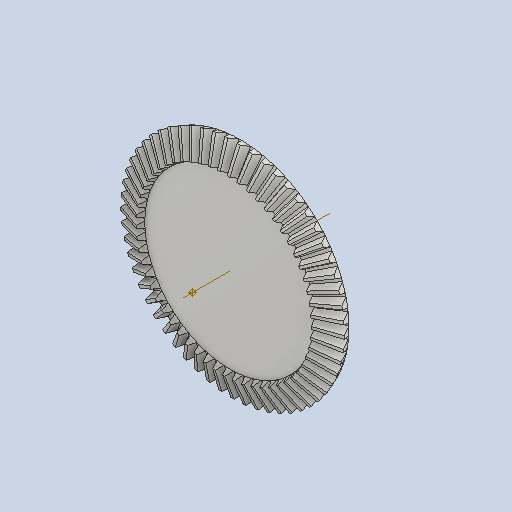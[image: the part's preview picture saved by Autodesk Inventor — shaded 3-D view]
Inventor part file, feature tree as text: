
AUTODESK INVENTOR PART (.ipt)
format: ipt  version: 2023 (Build 270158030, 158C)  size: 857,088 bytes
history: native  units: mm
features: other x24, loft x2, pattern_circular x2, sketch x1
ambient origin geometry x6: Origin, XZ Plane, X Axis, Y Axis, Z Axis, Center Point
bodies: Solid1 (feature_tree)
feature tree (29):
  other  "Top Point"
  other  "Mesh Plane2"
  other  "Teeth Body"
  other  "Start Point"
  other  "Tooth Plane"
  other  "Start Sketch"
  other  "End Point"
  other  "3D Sketch Right"
  other  "End Plane Right"
  loft  "Loft Right"
  pattern_circular  "Circular Pattern Right"  [2 undecoded]
  other  "3D Sketch Left"
  other  "End Plane Left"
  loft  "Loft Left"
  pattern_circular  "Circular Pattern Left"  [2 undecoded]
  other  "Fix Body"
  other  "Mesh Plane"
  other  "Top Plane"
  other  "Teeth Body Sketch"
  other  "End Plane"
  other  "End Sketch"
  other  "Helical Curve Left"
  other  "End Sketch Left"
  other  "Body Sketch"
  sketch  "Sketch6"  dims[d0=171.0mm d1=168.305803mm d2=173.245164mm d3=20.0mm d4=31.717949mm d5=90.0deg d7=79.194946mm d8=76.874908mm d9=201.595668mm d11=20.33mm d12=61.732197mm d15=59.923736mm d16=157.143153mm d17=0.0mm d18=90.0deg d19=0.0mm d20=90.0deg d21=570.0mm d22=360.0deg d26=492.398605mm d27=7.607365mm d28=171.0mm d29=-11.872688mm d30=61.732197mm d31=59.923736mm d32=157.143153mm d35=0.0mm d37=0.0mm d39=0.0mm d40=90.0deg d41=570.0mm d42=360.0deg d46=90.0deg d47=90.0deg d48=0.0mm d49=0.0mm d50=90.0deg d51=0.551157mm d52=0.0mm d53=0.0mm d54=0.0mm d56=25.418305mm d57=233.471083mm d58=224.099083mm d59=181.989933mm d60=174.68449mm d61=181.989933mm d62=174.68449mm d65=492.398605mm d66=31.5mm d67=171.0mm d68=-11.872688mm d69=7.607365mm d70=59.923736mm d71=157.143153mm d72=61.732197mm d73=174.68449mm d74=181.989933mm d75=0.0mm d77=0.0mm d79=0.0mm d80=90.0deg d81=570.0mm d82=360.0deg d84=10.0mm d85=20.0mm d86=20.0mm d87=10.0mm d88=0.0mm d89=0.0mm d90=90.0deg d91=90.0deg d92=90.0deg d93=90.0deg]
  other  "Srf1"
  other  "Helical Curve Right"
  other  "End Sketch Right"
  other  "Pitch Diameter"
note: 4 required parameter values undecoded (feature->parameter linkage not recoverable at this tier; creation-order binding heuristic only, values carry confidence <= 0.55)
